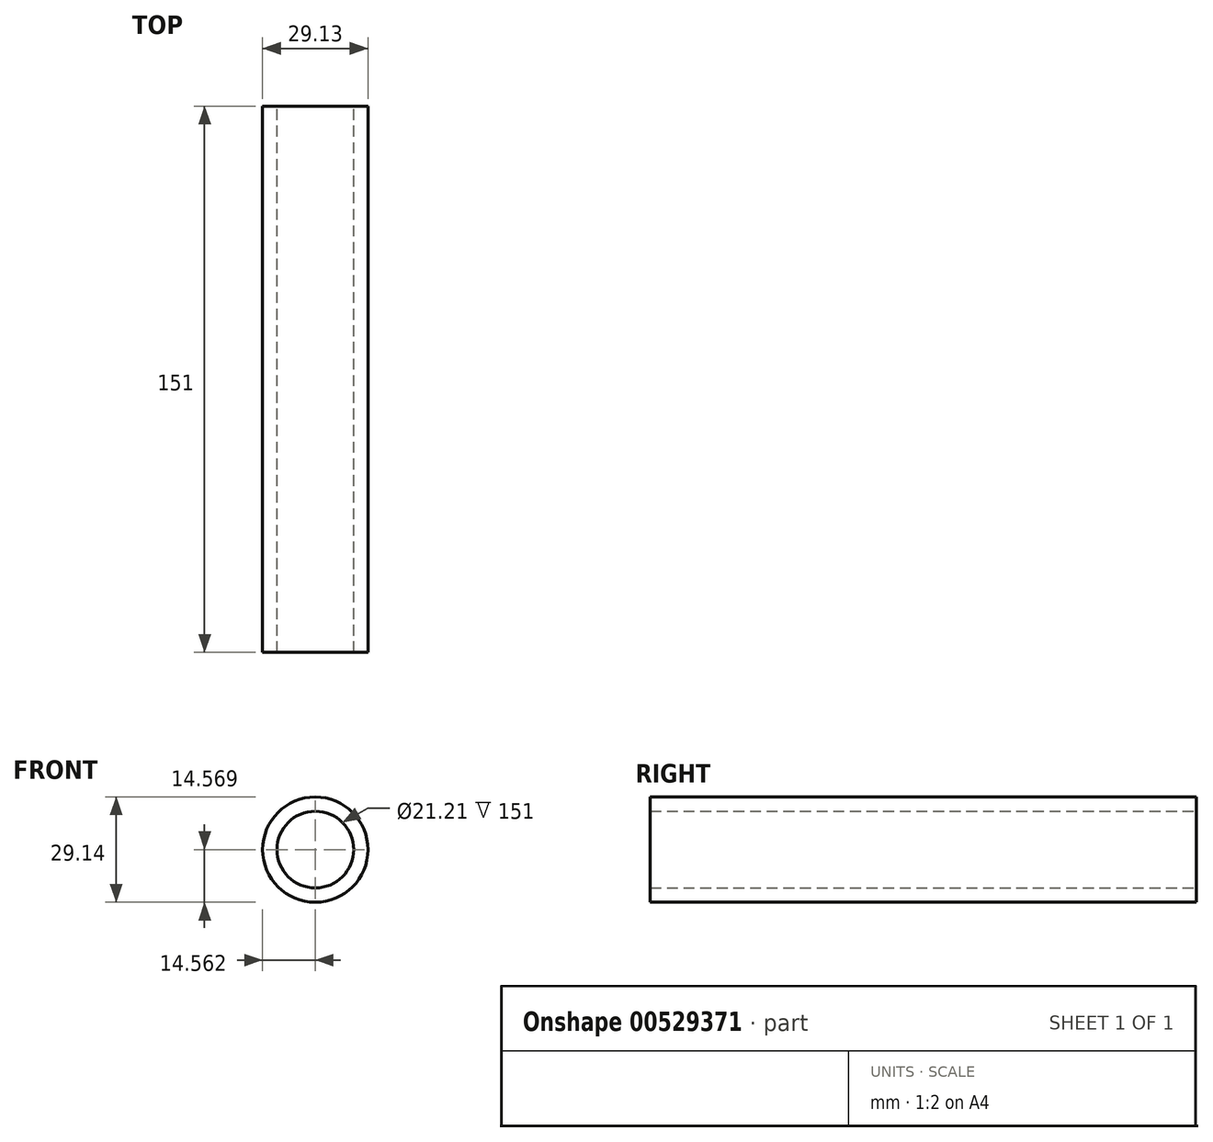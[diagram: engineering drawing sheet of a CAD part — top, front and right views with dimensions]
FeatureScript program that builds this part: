
annotation { "Feature Type Name" : "Feature", "Feature Type Description" : "" }
export const myFeature = defineFeature(function(context is Context, id is Id, definition is map)
    precondition{}
    {
        {
            var Q0;
            Q0=qCreatedBy(makeId("Front.planeOp"),FACE);
            var sketch = newSketch(context, id + "F0", { "sketchPlane" : qUnion([Q0])});
            skCircle(sketch, "E0", {"center": v(-0.46, 0.23) * mm, "radius": 14.57 * mm});
            skCircle(sketch, "E1", {"center": v(-0.46, 0.23) * mm, "radius": 10.6 * mm});
            skSolve(sketch);
        }
        {
            var Q0;
            Q0 = qSketchRegion(id + "F0", true);
            extrude(context, id + "F1", {"entities" : qUnion([Q0]), "depth" : 151 * mm, "offsetDistance" : 25 * mm});
        }
    });
